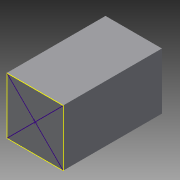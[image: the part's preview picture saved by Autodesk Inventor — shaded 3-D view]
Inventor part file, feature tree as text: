
AUTODESK INVENTOR PART (.ipt)
format: ipt  version: 2013 (Build 170138000, 138)  size: 88,064 bytes
history: native  units: mm
features: sketch x3, other x1, extrude x1, revolve x1
ambient origin geometry x8: Origin, YZ Plane, XZ Plane, XY Plane, X Axis, Y Axis, Z Axis, Center Point
feature tree (6):
  other  "ソリッド1"
  extrude  "押し出し1"  Depth=20.0mm
  revolve  "回転1"
  sketch  "スケッチ3"
  sketch  "スケッチ1"
  sketch  "スケッチ2"
